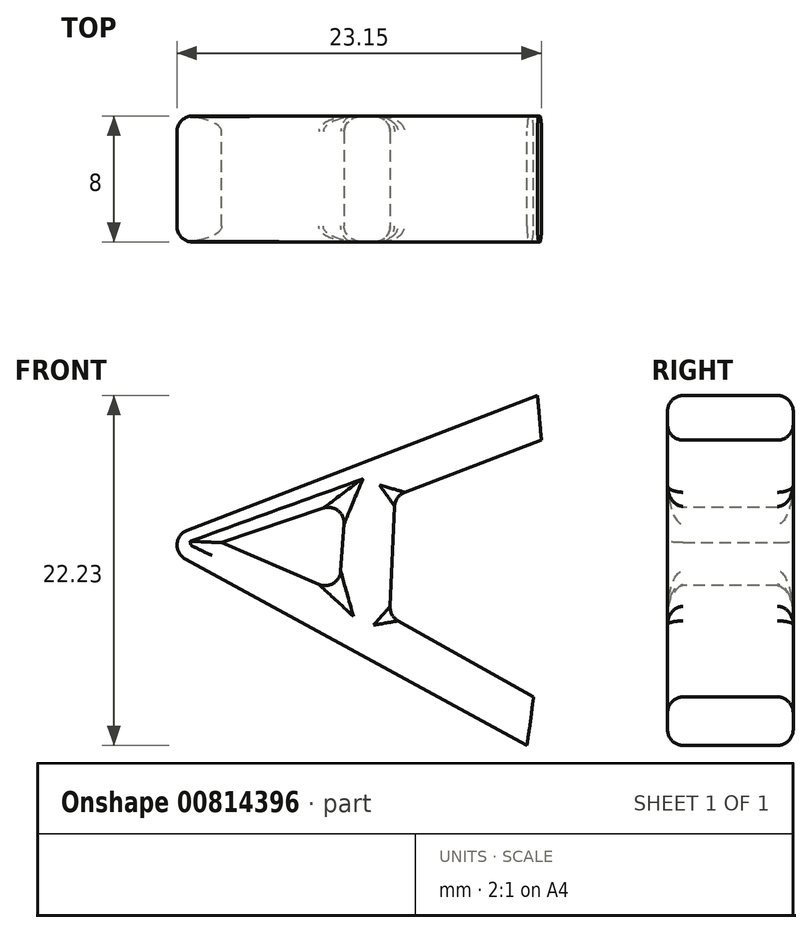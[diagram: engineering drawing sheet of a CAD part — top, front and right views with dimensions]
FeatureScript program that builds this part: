
annotation { "Feature Type Name" : "Feature", "Feature Type Description" : "" }
export const myFeature = defineFeature(function(context is Context, id is Id, definition is map)
    precondition{}
    {
        {
            var Q0;
            Q0=qCreatedBy(makeId("Front.planeOp"),FACE);
            var sketch = newSketch(context, id + "F0", { "sketchPlane" : qUnion([Q0])});
            skLineSegment(sketch, "E0", {"start": v(-13.99, 10.74) * mm, "end": v(-38.26, 1.4) * mm});
            skLineSegment(sketch, "E1", {"start": v(-38.26, 1.4) * mm, "end": v(-14.65, -11.5) * mm});
            skLineSegment(sketch, "E2", {"start": v(-14.65, -11.5) * mm, "end": v(-14.24, -8.4) * mm});
            skLineSegment(sketch, "E3", {"start": v(-14.24, -8.4) * mm, "end": v(-23.37, -3.27) * mm});
            skLineSegment(sketch, "E4", {"start": v(-23.37, -3.27) * mm, "end": v(-23.04, 4.36) * mm});
            skLineSegment(sketch, "E5", {"start": v(-23.04, 4.36) * mm, "end": v(-13.74, 7.9) * mm});
            skLineSegment(sketch, "E6", {"start": v(-13.74, 7.9) * mm, "end": v(-13.99, 10.74) * mm});
            skLineSegment(sketch, "E7", {"start": v(-26.17, 4.07) * mm, "end": v(-26.58, -1.81) * mm});
            skLineSegment(sketch, "E8", {"start": v(-26.58, -1.81) * mm, "end": v(-34.05, 1.4) * mm});
            skLineSegment(sketch, "E9", {"start": v(-34.05, 1.4) * mm, "end": v(-26.17, 4.07) * mm});
            skSolve(sketch);
        }
        {
            var Q0;
            Q0=makeQuery(id+"F0.imprint","IMPRINT",FACE,{"disambiguationData":[TD([[makeQuery(id+"F0.imprint","IMPRINT",EDGE,{"derivedFrom":sQuery(id+"F0.wireOp",EDGE,"E0")}),1.0]])]});
            extrude(context, id + "F1", {"entities" : qUnion([Q0]), "depth" : 8 * mm, "offsetDistance" : 25.4 * mm});
        }
        {
            var Q0;
            Q0=makeQuery(id+"F1.opExtrude","CAP_EDGE",EDGE,{"disambiguationData":[OSD([sQuery(id+"F0.wireOp",EDGE,"E7")])],"isStart":false});
            var Q1;
            Q1=makeQuery(id+"F1.opExtrude","CAP_EDGE",EDGE,{"disambiguationData":[OSD([sQuery(id+"F0.wireOp",EDGE,"E9")])],"isStart":false});
            var Q2;
            Q2=makeQuery(id+"F1.opExtrude","CAP_EDGE",EDGE,{"disambiguationData":[OSD([sQuery(id+"F0.wireOp",EDGE,"E8")])],"isStart":false});
            var Q3;
            Q3=makeQuery(id+"F1.opExtrude","CAP_EDGE",EDGE,{"disambiguationData":[OSD([sQuery(id+"F0.wireOp",EDGE,"E0")])],"isStart":false});
            var Q4;
            Q4=makeQuery(id+"F1.opExtrude","CAP_EDGE",EDGE,{"disambiguationData":[OSD([sQuery(id+"F0.wireOp",EDGE,"E1")])],"isStart":false});
            var Q5;
            Q5=makeQuery(id+"F1.opExtrude","CAP_EDGE",EDGE,{"disambiguationData":[OSD([sQuery(id+"F0.wireOp",EDGE,"E5")])],"isStart":false});
            var Q6;
            Q6=makeQuery(id+"F1.opExtrude","CAP_EDGE",EDGE,{"disambiguationData":[OSD([sQuery(id+"F0.wireOp",EDGE,"E4")])],"isStart":false});
            var Q7;
            Q7=makeQuery(id+"F1.opExtrude","CAP_EDGE",EDGE,{"disambiguationData":[OSD([sQuery(id+"F0.wireOp",EDGE,"E3")])],"isStart":false});
            var Q8;
            Q8=makeQuery(id+"F1.opExtrude","CAP_EDGE",EDGE,{"disambiguationData":[OSD([sQuery(id+"F0.wireOp",EDGE,"E1")])],"isStart":true});
            var Q9;
            Q9=makeQuery(id+"F1.opExtrude","CAP_EDGE",EDGE,{"disambiguationData":[OSD([sQuery(id+"F0.wireOp",EDGE,"E0")])],"isStart":true});
            var Q10;
            Q10=makeQuery(id+"F1.opExtrude","SWEPT_EDGE",EDGE,{"disambiguationData":[OSD([sQuery(id+"F0.wireOp",EDGE,"E0"),sQuery(id+"F0.wireOp",EDGE,"E1")])]});
            var Q11;
            Q11=makeQuery(id+"F1.opExtrude","CAP_EDGE",EDGE,{"disambiguationData":[OSD([sQuery(id+"F0.wireOp",EDGE,"E9")])],"isStart":true});
            var Q12;
            Q12=makeQuery(id+"F1.opExtrude","CAP_EDGE",EDGE,{"disambiguationData":[OSD([sQuery(id+"F0.wireOp",EDGE,"E8")])],"isStart":true});
            var Q13;
            Q13=makeQuery(id+"F1.opExtrude","CAP_EDGE",EDGE,{"disambiguationData":[OSD([sQuery(id+"F0.wireOp",EDGE,"E7")])],"isStart":true});
            var Q14;
            Q14=makeQuery(id+"F1.opExtrude","CAP_EDGE",EDGE,{"disambiguationData":[OSD([sQuery(id+"F0.wireOp",EDGE,"E4")])],"isStart":true});
            var Q15;
            Q15=makeQuery(id+"F1.opExtrude","CAP_EDGE",EDGE,{"disambiguationData":[OSD([sQuery(id+"F0.wireOp",EDGE,"E3")])],"isStart":true});
            var Q16;
            Q16=makeQuery(id+"F1.opExtrude","CAP_EDGE",EDGE,{"disambiguationData":[OSD([sQuery(id+"F0.wireOp",EDGE,"E5")])],"isStart":true});
            fillet(context, id + "F2", {"entities" : qUnion([Q0, Q1, Q2, Q3, Q4, Q5, Q6, Q7, Q8, Q9, Q10, Q11, Q12, Q13, Q14, Q15, Q16]), "radius" : 1 * mm, "tangentPropagation" : true, "allowEdgeOverflow" : false});
        }
        {
            var Q0;
            Q0=makeQuery(id+"F1.opExtrude","SWEPT_EDGE",EDGE,{"disambiguationData":[OSD([sQuery(id+"F0.wireOp",EDGE,"E4"),sQuery(id+"F0.wireOp",EDGE,"E5")])]});
            var Q1;
            Q1=makeQuery(id+"F1.opExtrude","SWEPT_EDGE",EDGE,{"disambiguationData":[OSD([sQuery(id+"F0.wireOp",EDGE,"E3"),sQuery(id+"F0.wireOp",EDGE,"E4")])]});
            var Q2;
            Q2=makeQuery(id+"F1.opExtrude","SWEPT_EDGE",EDGE,{"disambiguationData":[OSD([sQuery(id+"F0.wireOp",EDGE,"E7"),sQuery(id+"F0.wireOp",EDGE,"E8")])]});
            var Q3;
            Q3=makeQuery(id+"F1.opExtrude","SWEPT_EDGE",EDGE,{"disambiguationData":[OSD([sQuery(id+"F0.wireOp",EDGE,"E7"),sQuery(id+"F0.wireOp",EDGE,"E9")])]});
            fillet(context, id + "F3", {"entities" : qUnion([Q0, Q1, Q2, Q3]), "radius" : 1 * mm, "tangentPropagation" : true, "allowEdgeOverflow" : false});
        }
    });
